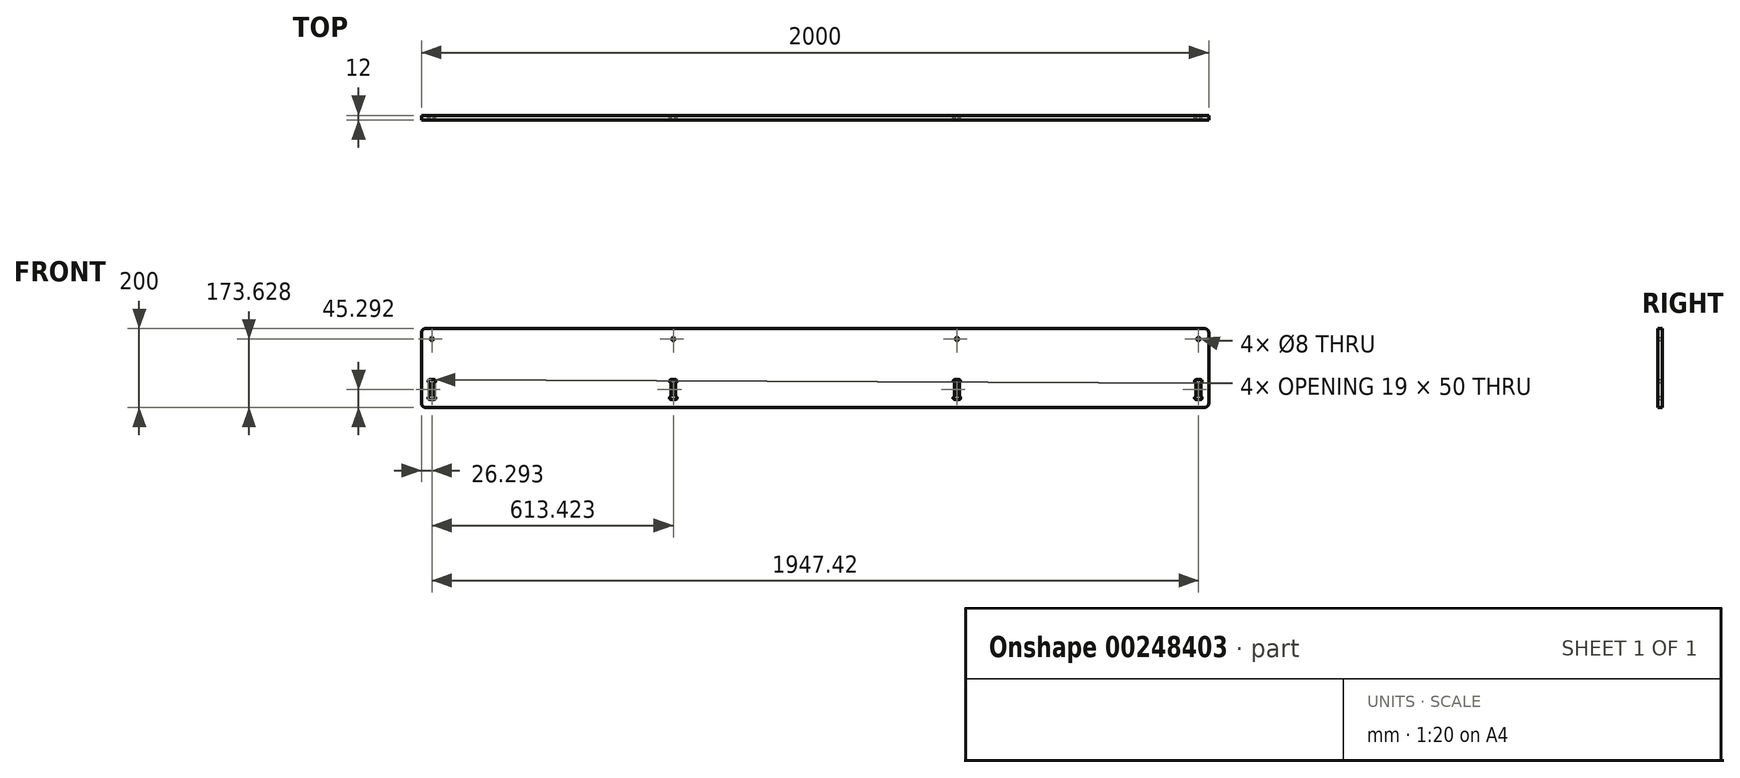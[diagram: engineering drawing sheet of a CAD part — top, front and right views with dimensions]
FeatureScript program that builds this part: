
annotation { "Feature Type Name" : "Feature", "Feature Type Description" : "" }
export const myFeature = defineFeature(function(context is Context, id is Id, definition is map)
    precondition{}
    {
        {
            var Q0;
            Q0=qCreatedBy(makeId("Front.planeOp"),FACE);
            var sketch = newSketch(context, id + "F0", { "sketchPlane" : qUnion([Q0])});
            skLineSegment(sketch, "E0.bottom", {"start": v(-931.2, 124.3) * mm, "end": v(1048.8, 124.3) * mm});
            skLineSegment(sketch, "E0.top", {"start": v(-931.2, -75.7) * mm, "end": v(1048.8, -75.7) * mm});
            skLineSegment(sketch, "E0.left", {"start": v(-941.2, 114.3) * mm, "end": v(-941.2, -65.7) * mm});
            skLineSegment(sketch, "E0.right", {"start": v(1058.8, 114.3) * mm, "end": v(1058.8, -65.7) * mm});
            skPoint(sketch, "E1.visualSharp", {"position": v(-941.2, 124.3) * mm});
            skArc(sketch, "E1.filletArc", {"start": v(-931.2, 124.3) * mm, "mid": v(-938.27, 121.37) * mm, "end": v(-941.2, 114.3) * mm});
            skPoint(sketch, "E2.visualSharp", {"position": v(-941.2, -75.7) * mm});
            skArc(sketch, "E2.filletArc", {"start": v(-941.2, -65.7) * mm, "mid": v(-938.27, -72.77) * mm, "end": v(-931.2, -75.7) * mm});
            skPoint(sketch, "E3.visualSharp", {"position": v(1058.8, 124.3) * mm});
            skArc(sketch, "E3.filletArc", {"start": v(1058.8, 114.3) * mm, "mid": v(1055.88, 121.37) * mm, "end": v(1048.8, 124.3) * mm});
            skPoint(sketch, "E4.visualSharp", {"position": v(1058.8, -75.7) * mm});
            skArc(sketch, "E4.filletArc", {"start": v(1048.8, -75.7) * mm, "mid": v(1055.88, -72.77) * mm, "end": v(1058.8, -65.7) * mm});
            skLineSegment(sketch, "E5.top", {"start": v(-902.9, -75.7) * mm, "end": v(-920.9, -75.7) * mm});
            skLineSegment(sketch, "E6.top", {"start": v(1038.52, -75.7) * mm, "end": v(1058.8, -75.7) * mm, "construction": true});
            skLineSegment(sketch, "E6.right", {"start": v(1058.8, -5.4) * mm, "end": v(1058.8, -75.7) * mm, "construction": true});
            skLineSegment(sketch, "E7", {"start": v(-920.9, -5.4) * mm, "end": v(-908.9, -5.4) * mm});
            skLineSegment(sketch, "E8", {"start": v(-920.9, -55.4) * mm, "end": v(-908.9, -55.4) * mm});
            skArc(sketch, "E9", {"start": v(-908.9, -55.4) * mm, "mid": v(-905.4, -51.9) * mm, "end": v(-908.9, -48.4) * mm});
            skArc(sketch, "E10", {"start": v(-920.9, -48.4) * mm, "mid": v(-924.4, -51.9) * mm, "end": v(-920.9, -55.4) * mm});
            skArc(sketch, "E11", {"start": v(-908.9, -12.4) * mm, "mid": v(-905.4, -8.9) * mm, "end": v(-908.9, -5.4) * mm});
            skArc(sketch, "E12", {"start": v(-920.9, -5.4) * mm, "mid": v(-924.4, -8.9) * mm, "end": v(-920.9, -12.4) * mm});
            skLineSegment(sketch, "E13", {"start": v(-920.9, -55.4) * mm, "end": v(-920.9, -55.48) * mm});
            skLineSegment(sketch, "E14.trimOffspring", {"start": v(-920.9, -12.4) * mm, "end": v(-920.9, -48.4) * mm});
            skLineSegment(sketch, "E15.0", {"start": v(-908.9, -12.4) * mm, "end": v(-908.9, -48.4) * mm});
            skLineSegment(sketch, "E16.0", {"start": v(58.8, -5.4) * mm, "end": v(58.8, -55.48) * mm, "construction": true});
            skLineSegment(sketch, "E17.MirrorCS", {"start": v(1038.52, -12.4) * mm, "end": v(1038.52, -48.4) * mm});
            skArc(sketch, "E18.MirrorCS", {"start": v(1038.52, -5.4) * mm, "mid": v(1042.02, -8.9) * mm, "end": v(1038.52, -12.4) * mm});
            skLineSegment(sketch, "E19.MirrorCS", {"start": v(1038.52, -5.4) * mm, "end": v(1026.52, -5.4) * mm});
            skArc(sketch, "E20.MirrorCS", {"start": v(1026.52, -12.4) * mm, "mid": v(1023.02, -8.9) * mm, "end": v(1026.52, -5.4) * mm});
            skLineSegment(sketch, "E21.MirrorCS", {"start": v(1026.52, -12.4) * mm, "end": v(1026.52, -48.4) * mm});
            skArc(sketch, "E22.MirrorCS", {"start": v(1026.52, -55.4) * mm, "mid": v(1023.02, -51.9) * mm, "end": v(1026.52, -48.4) * mm});
            skLineSegment(sketch, "E23.MirrorCS", {"start": v(1038.52, -55.4) * mm, "end": v(1026.52, -55.4) * mm});
            skArc(sketch, "E24.MirrorCS", {"start": v(1038.52, -48.4) * mm, "mid": v(1042.02, -51.9) * mm, "end": v(1038.52, -55.4) * mm});
            skLineSegment(sketch, "E25.0", {"start": v(-608.2, 17.38) * mm, "end": v(-608.2, -65.7) * mm, "construction": true});
            skLineSegment(sketch, "E26.MirrorCS", {"start": v(-295.48, -55.4) * mm, "end": v(-295.48, -55.48) * mm});
            skArc(sketch, "E27.MirrorCS", {"start": v(-295.48, -48.4) * mm, "mid": v(-291.98, -51.9) * mm, "end": v(-295.48, -55.4) * mm});
            skArc(sketch, "E28.MirrorCS", {"start": v(-295.48, -5.4) * mm, "mid": v(-291.98, -8.9) * mm, "end": v(-295.48, -12.4) * mm});
            skArc(sketch, "E29.MirrorCS", {"start": v(-307.48, -12.4) * mm, "mid": v(-310.98, -8.9) * mm, "end": v(-307.48, -5.4) * mm});
            skArc(sketch, "E30.MirrorCS", {"start": v(-307.48, -55.4) * mm, "mid": v(-310.98, -51.9) * mm, "end": v(-307.48, -48.4) * mm});
            skLineSegment(sketch, "E31.MirrorCS", {"start": v(-295.48, -5.4) * mm, "end": v(-307.48, -5.4) * mm});
            skLineSegment(sketch, "E32.MirrorCS", {"start": v(-307.48, -12.4) * mm, "end": v(-307.48, -48.4) * mm});
            skLineSegment(sketch, "E33.MirrorCS", {"start": v(-295.48, -12.4) * mm, "end": v(-295.48, -48.4) * mm});
            skLineSegment(sketch, "E34.MirrorCS", {"start": v(-295.48, -55.4) * mm, "end": v(-307.48, -55.4) * mm});
            skLineSegment(sketch, "E35.MirrorCS", {"start": v(413.1, -55.4) * mm, "end": v(413.1, -55.48) * mm});
            skArc(sketch, "E36.MirrorCS", {"start": v(413.1, -48.4) * mm, "mid": v(409.6, -51.9) * mm, "end": v(413.1, -55.4) * mm});
            skLineSegment(sketch, "E37.MirrorCS", {"start": v(413.1, -55.4) * mm, "end": v(425.1, -55.4) * mm});
            skArc(sketch, "E38.MirrorCS", {"start": v(425.1, -12.4) * mm, "mid": v(428.6, -8.9) * mm, "end": v(425.1, -5.4) * mm});
            skArc(sketch, "E39.MirrorCS", {"start": v(413.1, -5.4) * mm, "mid": v(409.6, -8.9) * mm, "end": v(413.1, -12.4) * mm});
            skArc(sketch, "E40.MirrorCS", {"start": v(425.1, -55.4) * mm, "mid": v(428.6, -51.9) * mm, "end": v(425.1, -48.4) * mm});
            skLineSegment(sketch, "E41.MirrorCS", {"start": v(413.1, -5.4) * mm, "end": v(425.1, -5.4) * mm});
            skLineSegment(sketch, "E42.MirrorCS", {"start": v(425.1, -12.4) * mm, "end": v(425.1, -48.4) * mm});
            skLineSegment(sketch, "E43.MirrorCS", {"start": v(413.1, -12.4) * mm, "end": v(413.1, -48.4) * mm});
            skLineSegment(sketch, "E44", {"start": v(-914.9, -5.4) * mm, "end": v(-914.9, 124.3) * mm, "construction": true});
            skLineSegment(sketch, "E45.bottom", {"start": v(-941.2, 124.3) * mm, "end": v(-914.9, 124.3) * mm, "construction": true});
            skLineSegment(sketch, "E45.top", {"start": v(-941.2, 97.93) * mm, "end": v(-914.9, 97.93) * mm, "construction": true});
            skLineSegment(sketch, "E45.left", {"start": v(-941.2, 124.3) * mm, "end": v(-941.2, 97.93) * mm, "construction": true});
            skLineSegment(sketch, "E45.right", {"start": v(-914.9, 124.3) * mm, "end": v(-914.9, 97.93) * mm, "construction": true});
            skCircle(sketch, "E46", {"center": v(-914.9, 97.93) * mm, "radius": 4 * mm});
            skCircle(sketch, "E47.MirrorC", {"center": v(-301.48, 97.93) * mm, "radius": 4 * mm});
            skCircle(sketch, "E48.MirrorC", {"center": v(1032.52, 97.93) * mm, "radius": 4 * mm});
            skCircle(sketch, "E49.MirrorC", {"center": v(419.1, 97.93) * mm, "radius": 4 * mm});
            skSolve(sketch);
        }
        {
            var Q0;
            Q0=makeQuery(id+"F0.imprint","IMPRINT",FACE,{"disambiguationData":[TD([[makeQuery(id+"F0.imprint","IMPRINT",EDGE,{"derivedFrom":sQuery(id+"F0.wireOp",EDGE,"E0.bottom")}),-1.0]])]});
            extrude(context, id + "F1", {"entities" : qUnion([Q0]), "depth" : 12 * mm});
        }
    });
